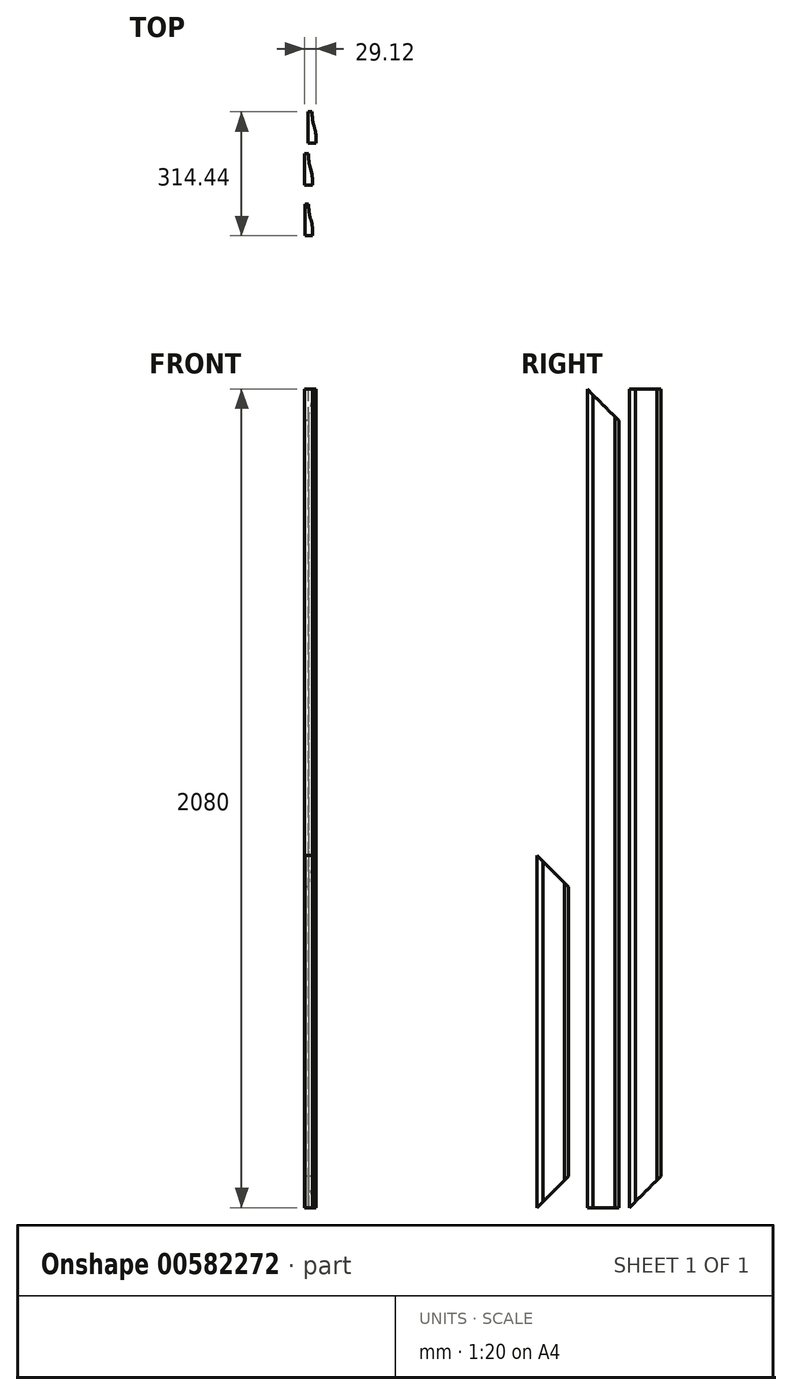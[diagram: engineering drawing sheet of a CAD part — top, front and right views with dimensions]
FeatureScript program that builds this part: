
annotation { "Feature Type Name" : "Feature", "Feature Type Description" : "" }
export const myFeature = defineFeature(function(context is Context, id is Id, definition is map)
    precondition{}
    {
        {
            var Q0;
            Q0=qCreatedBy(makeId("Top.planeOp"),FACE);
            var sketch = newSketch(context, id + "F0", { "sketchPlane" : qUnion([Q0])});
            skLineSegment(sketch, "E0", {"start": v(0, 0) * mm, "end": v(0, 80) * mm});
            skLineSegment(sketch, "E1", {"start": v(0, 80) * mm, "end": v(10, 80) * mm});
            skLineSegment(sketch, "E2", {"start": v(0, 0) * mm, "end": v(20, 0) * mm});
            skLineSegment(sketch, "E3", {"start": v(10, 80) * mm, "end": v(10, 70) * mm});
            skLineSegment(sketch, "E4", {"start": v(20, 0) * mm, "end": v(20, 15) * mm});
            skFitSpline(sketch, "E5", {"points": [v(10, 70) * mm, v(20, 15) * mm], "startDerivative": vector(6.87, -92.18) * mm, "endDerivative": vector(8.95, -97.63) * mm});
            skLineSegment(sketch, "E6", {"start": v(9.12, 106.8) * mm, "end": v(9.12, 186.8) * mm});
            skLineSegment(sketch, "E7", {"start": v(9.12, 186.8) * mm, "end": v(19.12, 186.8) * mm});
            skLineSegment(sketch, "E8", {"start": v(9.12, 106.8) * mm, "end": v(29.12, 106.8) * mm});
            skLineSegment(sketch, "E9", {"start": v(19.12, 186.8) * mm, "end": v(19.12, 176.8) * mm});
            skLineSegment(sketch, "E10", {"start": v(29.12, 106.8) * mm, "end": v(29.12, 121.8) * mm});
            skFitSpline(sketch, "E11", {"points": [v(19.12, 176.8) * mm, v(29.12, 121.8) * mm], "startDerivative": vector(6.87, -92.18) * mm, "endDerivative": vector(8.95, -97.63) * mm});
            skLineSegment(sketch, "E12", {"start": v(0.34, -127.64) * mm, "end": v(0.34, -47.64) * mm});
            skLineSegment(sketch, "E13", {"start": v(0.34, -47.64) * mm, "end": v(10.34, -47.64) * mm});
            skLineSegment(sketch, "E14", {"start": v(0.34, -127.64) * mm, "end": v(20.34, -127.64) * mm});
            skLineSegment(sketch, "E15", {"start": v(10.34, -47.64) * mm, "end": v(10.34, -57.64) * mm});
            skLineSegment(sketch, "E16", {"start": v(20.34, -127.64) * mm, "end": v(20.34, -112.64) * mm});
            skFitSpline(sketch, "E17", {"points": [v(10.34, -57.64) * mm, v(20.34, -112.64) * mm], "startDerivative": vector(6.87, -92.18) * mm, "endDerivative": vector(8.95, -97.63) * mm});
            skSolve(sketch);
        }
        {
            var Q0;
            Q0=makeQuery(id+"F0.imprint","IMPRINT",FACE,{"disambiguationData":[TD([[makeQuery(id+"F0.imprint","IMPRINT",EDGE,{"derivedFrom":sQuery(id+"F0.wireOp",EDGE,"E0")}),-1.0]])]});
            extrude(context, id + "F1", {"entities" : qUnion([Q0]), "depth" : 2080 * mm, "offsetDistance" : 25 * mm});
        }
        {
            var Q0;
            Q0=makeQuery(id+"F0.imprint","IMPRINT",FACE,{"disambiguationData":[TD([[makeQuery(id+"F0.imprint","IMPRINT",EDGE,{"derivedFrom":sQuery(id+"F0.wireOp",EDGE,"E6")}),-1.0]])]});
            extrude(context, id + "F2", {"entities" : qUnion([Q0]), "depth" : 2080 * mm, "offsetDistance" : 25 * mm});
        }
        {
            var Q0;
            Q0=makeQuery(id+"F0.imprint","IMPRINT",FACE,{"disambiguationData":[TD([[makeQuery(id+"F0.imprint","IMPRINT",EDGE,{"derivedFrom":sQuery(id+"F0.wireOp",EDGE,"E12")}),-1.0]])]});
            extrude(context, id + "F3", {"entities" : qUnion([Q0]), "depth" : 895 * mm, "offsetDistance" : 25 * mm});
        }
        {
            var Q0;
            Q0=makeQuery(id+"F2.opExtrude","SWEPT_FACE",FACE,{"disambiguationData":[OSD([sQuery(id+"F0.wireOp",EDGE,"E6")])]});
            var sketch = newSketch(context, id + "F4", { "sketchPlane" : qUnion([Q0])});
            skLineSegment(sketch, "E18", {"start": v(-106.8, 0) * mm, "end": v(-186.8, 0) * mm});
            skLineSegment(sketch, "E19", {"start": v(-186.8, 0) * mm, "end": v(-186.8, 80) * mm});
            skLineSegment(sketch, "E20", {"start": v(-186.8, 80) * mm, "end": v(-106.8, 0) * mm});
            skSolve(sketch);
        }
        {
            var Q0;
            Q0=makeQuery(id+"F1.opExtrude","SWEPT_FACE",FACE,{"disambiguationData":[OSD([sQuery(id+"F0.wireOp",EDGE,"E0")])]});
            var sketch = newSketch(context, id + "F5", { "sketchPlane" : qUnion([Q0])});
            skLineSegment(sketch, "E21", {"start": v(0, 2080) * mm, "end": v(-80, 2080) * mm});
            skLineSegment(sketch, "E22", {"start": v(-80, 2080) * mm, "end": v(-80, 2000) * mm});
            skLineSegment(sketch, "E23", {"start": v(-80, 2000) * mm, "end": v(0, 2080) * mm});
            skSolve(sketch);
        }
        {
            var Q0;
            Q0=makeQuery(id+"F3.opExtrude","SWEPT_FACE",FACE,{"disambiguationData":[OSD([sQuery(id+"F0.wireOp",EDGE,"E12")])]});
            var sketch = newSketch(context, id + "F6", { "sketchPlane" : qUnion([Q0])});
            skLineSegment(sketch, "E24", {"start": v(127.64, 895) * mm, "end": v(47.64, 895) * mm});
            skLineSegment(sketch, "E25", {"start": v(47.64, 895) * mm, "end": v(47.64, 815) * mm});
            skLineSegment(sketch, "E26", {"start": v(47.64, 815) * mm, "end": v(127.64, 895) * mm});
            skLineSegment(sketch, "E27", {"start": v(127.64, 0) * mm, "end": v(47.64, 0) * mm});
            skLineSegment(sketch, "E28", {"start": v(47.64, 0) * mm, "end": v(47.64, 80) * mm});
            skLineSegment(sketch, "E29", {"start": v(47.64, 80) * mm, "end": v(127.64, 0) * mm});
            skSolve(sketch);
        }
        {
            var Q0;
            Q0=makeQuery(id+"F4.imprint","IMPRINT",FACE,{"disambiguationData":[TD([[makeQuery(id+"F4.imprint","IMPRINT",EDGE,{"derivedFrom":sQuery(id+"F4.wireOp",EDGE,"E18")}),-1.0]])]});
            extrude(context, id + "F7", {"entities" : qUnion([Q0]), "operationType" : NewBodyOperationType.REMOVE, "oppositeDirection" : true, "depth" : 25 * mm, "offsetDistance" : 25 * mm});
        }
        {
            var Q0;
            Q0=makeQuery(id+"F5.imprint","IMPRINT",FACE,{"disambiguationData":[TD([[makeQuery(id+"F5.imprint","IMPRINT",EDGE,{"derivedFrom":sQuery(id+"F5.wireOp",EDGE,"E21")}),1.0]])]});
            extrude(context, id + "F8", {"entities" : qUnion([Q0]), "operationType" : NewBodyOperationType.REMOVE, "oppositeDirection" : true, "depth" : 25 * mm, "offsetDistance" : 25 * mm});
        }
        {
            var Q0;
            Q0=makeQuery(id+"F6.imprint","IMPRINT",FACE,{"disambiguationData":[TD([[makeQuery(id+"F6.imprint","IMPRINT",EDGE,{"derivedFrom":sQuery(id+"F6.wireOp",EDGE,"E24")}),1.0]])]});
            var Q1;
            Q1=makeQuery(id+"F6.imprint","IMPRINT",FACE,{"disambiguationData":[TD([[makeQuery(id+"F6.imprint","IMPRINT",EDGE,{"derivedFrom":sQuery(id+"F6.wireOp",EDGE,"E27")}),-1.0]])]});
            extrude(context, id + "F9", {"entities" : qUnion([Q0, Q1]), "operationType" : NewBodyOperationType.REMOVE, "oppositeDirection" : true, "depth" : 25 * mm, "offsetDistance" : 25 * mm});
        }
    });
